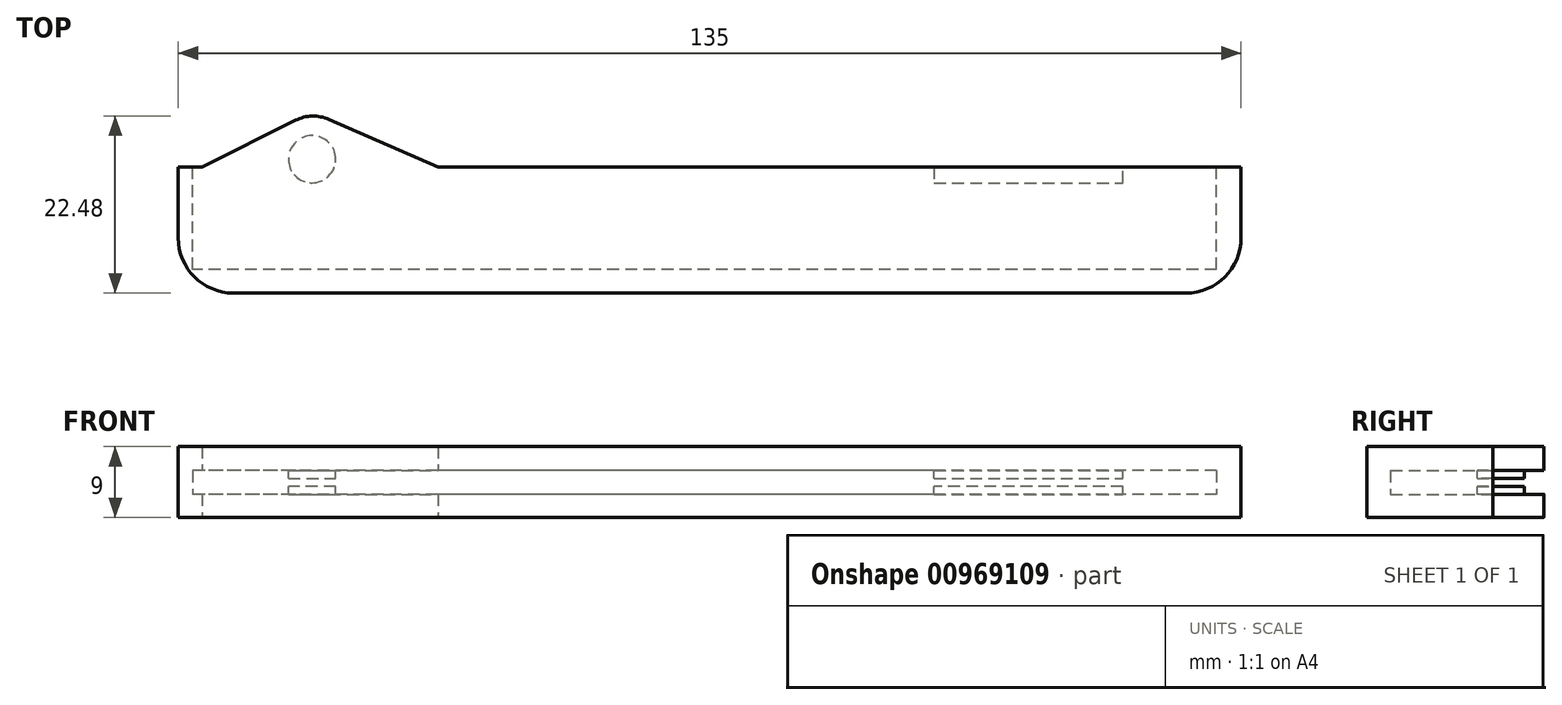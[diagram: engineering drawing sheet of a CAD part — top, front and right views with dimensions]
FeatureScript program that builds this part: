
annotation { "Feature Type Name" : "Feature", "Feature Type Description" : "" }
export const myFeature = defineFeature(function(context is Context, id is Id, definition is map)
    precondition{}
    {
        {
            var Q0;
            Q0=qCreatedBy(makeId("Top.planeOp"),FACE);
            var sketch = newSketch(context, id + "F0", { "sketchPlane" : qUnion([Q0])});
            skLineSegment(sketch, "E0.bottom", {"start": v(-67.5, 11.5) * mm, "end": v(67.5, 11.5) * mm});
            skLineSegment(sketch, "E0.top", {"start": v(-67.5, -11.5) * mm, "end": v(67.5, -11.5) * mm});
            skLineSegment(sketch, "E0.left", {"start": v(-67.5, 11.5) * mm, "end": v(-67.5, -11.5) * mm});
            skLineSegment(sketch, "E0.right", {"start": v(67.5, 11.5) * mm, "end": v(67.5, -11.5) * mm});
            skPoint(sketch, "E0.middle", {"position": v(0, 0) * mm});
            skLineSegment(sketch, "E1", {"start": v(67.5, 4.5) * mm, "end": v(-67.5, 4.5) * mm});
            skLineSegment(sketch, "E2", {"start": v(-50.5, 11.5) * mm, "end": v(-34.5, 4.5) * mm});
            skLineSegment(sketch, "E3", {"start": v(-50.5, 11.5) * mm, "end": v(-64.5, 4.5) * mm});
            skSolve(sketch);
        }
        {
            var Q0;
            {var subQ1=sQuery(id+"F0.wireOp",EDGE,"E0.top");Q0=makeQuery(id+"F0.imprint","IMPRINT",FACE,{"disambiguationData":[TD([[makeQuery(id+"F0.imprint","IMPRINT",EDGE,{"derivedFrom":subQ1}),1.0]])]});}
            var Q1;
            {var subQ2=sQuery(id+"F0.wireOp",EDGE,"E2");Q1=makeQuery(id+"F0.imprint","IMPRINT",FACE,{"disambiguationData":[TD([[makeQuery(id+"F0.imprint","IMPRINT",EDGE,{"derivedFrom":subQ2}),-1.0]])]});}
            extrude(context, id + "F1", {"entities" : qUnion([Q0, Q1]), "depth" : 9 * mm, "offsetDistance" : 25 * mm});
        }
        {
            var Q0;
            {var subQ0=sQuery(id+"F0.wireOp",EDGE,"E1");Q0=makeQuery(id+"F1.opExtrude","SWEPT_FACE",FACE,{"disambiguationData":[OSD([subQ0]),TDD([makeQuery(id+"F0.imprint","IMPRINT",EDGE,{"disambiguationData":[TD([[makeQuery(id+"F0.imprint","INTERSECT",VERTEX,{"derivedFrom":[sQuery(id+"F0.wireOp",EDGE,"E0.right"),subQ0]}),-1.0]])],"derivedFrom":subQ0})])]});}
            var sketch = newSketch(context, id + "F2", { "sketchPlane" : qUnion([Q0])});
            skLineSegment(sketch, "E4.bottom", {"start": v(-64.39, 5.94) * mm, "end": v(65.7, 5.94) * mm});
            skLineSegment(sketch, "E4.top", {"start": v(-64.39, 2.94) * mm, "end": v(65.7, 2.94) * mm});
            skLineSegment(sketch, "E4.left", {"start": v(-64.39, 5.94) * mm, "end": v(-64.39, 2.94) * mm});
            skLineSegment(sketch, "E4.right", {"start": v(65.7, 5.94) * mm, "end": v(65.7, 2.94) * mm});
            skSolve(sketch);
        }
        {
            var Q0;
            Q0 = qSketchRegion(id + "F2", true);
            extrude(context, id + "F3", {"entities" : qUnion([Q0]), "operationType" : NewBodyOperationType.REMOVE, "oppositeDirection" : true, "depth" : 13 * mm, "offsetDistance" : 25 * mm});
        }
        {
            var Q0;
            Q0=makeQuery(id+"F3.boolean.opBoolean","COPY",FACE,{"derivedFrom":makeQuery(id+"F3.opExtrude","CAP_FACE",FACE,{"disambiguationData":[OSD([sQuery(id+"F2.wireOp",EDGE,"E4.bottom"),sQuery(id+"F2.wireOp",EDGE,"E4.top"),sQuery(id+"F2.wireOp",EDGE,"E4.left"),sQuery(id+"F2.wireOp",EDGE,"E4.right")])],"isStart":false})});
            extrude(context, id + "F4", {"entities" : qUnion([Q0]), "operationType" : NewBodyOperationType.REMOVE, "depth" : 25 * mm, "offsetDistance" : 25 * mm});
        }
        {
            var Q0;
            {var subQ0=sQuery(id+"F2.wireOp",EDGE,"E4.bottom");Q0=makeQuery(id+"F4.boolean.opBoolean","MERGE",FACE,{"derivedFrom":[makeQuery(id+"F3.boolean.opBoolean","COPY",FACE,{"derivedFrom":makeQuery(id+"F3.opExtrude","SWEPT_FACE",FACE,{"disambiguationData":[OSD([subQ0])]})})],"fromTools":[makeQuery(id+"F4.opExtrude","SWEPT_FACE",FACE,{"disambiguationData":[OSD([subQ0])]})]});}
            var sketch = newSketch(context, id + "F5", { "sketchPlane" : qUnion([Q0])});
            skLineSegment(sketch, "E5", {"start": v(52.5, -4.5) * mm, "end": v(52.5, 7.04) * mm, "construction": true});
            skLineSegment(sketch, "E6", {"start": v(28.5, -4.5) * mm, "end": v(28.5, 11.64) * mm});
            skLineSegment(sketch, "E7", {"start": v(28.5, -2.5) * mm, "end": v(52.5, -2.5) * mm});
            skLineSegment(sketch, "E8.top", {"start": v(28.5, -4.5) * mm, "end": v(52.5, -4.5) * mm});
            skLineSegment(sketch, "E8.left", {"start": v(28.5, -2.5) * mm, "end": v(28.5, -4.5) * mm});
            skLineSegment(sketch, "E8.right", {"start": v(52.5, -2.5) * mm, "end": v(52.5, -4.5) * mm});
            skSolve(sketch);
        }
        {
            var Q0;
            {var subQ0=sQuery(id+"F5.wireOp",EDGE,"E7");Q0=makeQuery(id+"F5.imprint","IMPRINT",FACE,{"disambiguationData":[TD([[makeQuery(id+"F5.imprint","IMPRINT",EDGE,{"derivedFrom":subQ0}),-1.0]])]});}
            extrude(context, id + "F6", {"entities" : qUnion([Q0]), "operationType" : NewBodyOperationType.ADD, "depth" : 3 * mm, "offsetDistance" : 25 * mm});
        }
        {
            var Q0;
            {var subQ0=sQuery(id+"F0.wireOp",EDGE,"E1");Q0=makeQuery(id+"F6.boolean.opBoolean","MERGE",FACE,{"derivedFrom":[makeQuery(id+"F1.opExtrude","SWEPT_FACE",FACE,{"disambiguationData":[OSD([subQ0]),TDD([makeQuery(id+"F0.imprint","IMPRINT",EDGE,{"disambiguationData":[TD([[makeQuery(id+"F0.imprint","INTERSECT",VERTEX,{"derivedFrom":[sQuery(id+"F0.wireOp",EDGE,"E0.right"),subQ0]}),-1.0]])],"derivedFrom":subQ0})])]}),makeQuery(id+"F6.opExtrude","SWEPT_FACE",FACE,{"disambiguationData":[OSD([sQuery(id+"F5.wireOp",EDGE,"E8.top")])]})]});}
            var sketch = newSketch(context, id + "F7", { "sketchPlane" : qUnion([Q0])});
            skLineSegment(sketch, "E9", {"start": v(-52.5, 4.94) * mm, "end": v(-28.5, 4.94) * mm});
            skLineSegment(sketch, "E10", {"start": v(-28.5, 3.94) * mm, "end": v(-52.5, 3.94) * mm});
            skLineSegment(sketch, "E11", {"start": v(-28.5, 4.94) * mm, "end": v(65, 4.94) * mm});
            skLineSegment(sketch, "E12", {"start": v(65, 4.94) * mm, "end": v(65, 3.94) * mm});
            skLineSegment(sketch, "E13", {"start": v(65, 3.94) * mm, "end": v(-28.5, 3.94) * mm});
            skSolve(sketch);
        }
        {
            var Q0;
            {var subQ0=sQuery(id+"F2.wireOp",EDGE,"E4.bottom");Q0=makeQuery(id+"F4.boolean.opBoolean","MERGE",FACE,{"derivedFrom":[makeQuery(id+"F3.boolean.opBoolean","COPY",FACE,{"derivedFrom":makeQuery(id+"F3.opExtrude","SWEPT_FACE",FACE,{"disambiguationData":[OSD([subQ0])]})})],"fromTools":[makeQuery(id+"F4.opExtrude","SWEPT_FACE",FACE,{"disambiguationData":[OSD([subQ0])]})]});}
            var sketch = newSketch(context, id + "F8", { "sketchPlane" : qUnion([Q0])});
            skCircle(sketch, "E14", {"center": v(-50.5, -5.5) * mm, "radius": 3 * mm});
            skSolve(sketch);
        }
        {
            var Q0;
            Q0=makeQuery(id+"F8.imprint","IMPRINT",FACE,{"disambiguationData":[TD([[makeQuery(id+"F8.imprint","IMPRINT",EDGE,{"derivedFrom":sQuery(id+"F8.wireOp",EDGE,"E14")}),1.0]])]});
            extrude(context, id + "F9", {"entities" : qUnion([Q0]), "operationType" : NewBodyOperationType.ADD, "depth" : 4 * mm, "offsetDistance" : 25 * mm});
        }
        {
            var Q0;
            {var subQ0=sQuery(id+"F7.wireOp",EDGE,"E9");Q0=makeQuery(id+"F7.imprint","IMPRINT",FACE,{"disambiguationData":[TD([[makeQuery(id+"F7.imprint","IMPRINT",EDGE,{"derivedFrom":subQ0}),-1.0]])]});}
            var Q1;
            {var subQ0=sQuery(id+"F7.wireOp",EDGE,"E11");Q1=makeQuery(id+"F7.imprint","IMPRINT",FACE,{"disambiguationData":[TD([[makeQuery(id+"F7.imprint","IMPRINT",EDGE,{"derivedFrom":subQ0}),-1.0]])]});}
            extrude(context, id + "F10", {"entities" : qUnion([Q0, Q1]), "operationType" : NewBodyOperationType.REMOVE, "oppositeDirection" : true, "depth" : 10 * mm, "offsetDistance" : 25 * mm});
        }
        {
            var Q0;
            {var subQ0=sQuery(id+"F7.wireOp",EDGE,"E11");Q0=makeQuery(id+"F7.imprint","IMPRINT",FACE,{"disambiguationData":[TD([[makeQuery(id+"F7.imprint","IMPRINT",EDGE,{"derivedFrom":subQ0}),-1.0]])]});}
            extrude(context, id + "F11", {"entities" : qUnion([Q0]), "operationType" : NewBodyOperationType.REMOVE, "depth" : 25 * mm, "offsetDistance" : 25 * mm});
        }
        {
            var Q0;
            {var subQ0=sQuery(id+"F0.wireOp",EDGE,"E3");var subQ1=sQuery(id+"F2.wireOp",EDGE,"E4.top");var subQ2=sQuery(id+"F0.wireOp",EDGE,"E2");Q0=makeQuery(id+"F4.boolean.opBoolean","SPLIT",EDGE,{"disambiguationData":[TD([makeQuery(id+"F3.boolean.opBoolean","COPY",FACE,{"derivedFrom":makeQuery(id+"F3.opExtrude","SWEPT_FACE",FACE,{"disambiguationData":[OSD([subQ1])]})})])],"derivedFrom":makeQuery(id+"F1.opExtrude","SWEPT_EDGE",EDGE,{"disambiguationData":[OSD([sQuery(id+"F0.wireOp",EDGE,"E0.bottom"),subQ2,subQ0])]})});}
            var Q1;
            {var subQ0=sQuery(id+"F2.wireOp",EDGE,"E4.bottom");var subQ1=sQuery(id+"F0.wireOp",EDGE,"E3");var subQ2=sQuery(id+"F0.wireOp",EDGE,"E2");Q1=makeQuery(id+"F4.boolean.opBoolean","SPLIT",EDGE,{"disambiguationData":[TD([makeQuery(id+"F3.boolean.opBoolean","COPY",FACE,{"derivedFrom":makeQuery(id+"F3.opExtrude","SWEPT_FACE",FACE,{"disambiguationData":[OSD([subQ0])]})})])],"derivedFrom":makeQuery(id+"F1.opExtrude","SWEPT_EDGE",EDGE,{"disambiguationData":[OSD([sQuery(id+"F0.wireOp",EDGE,"E0.bottom"),subQ2,subQ1])]})});}
            fillet(context, id + "F12", {"entities" : qUnion([Q0, Q1]), "radius" : 5 * mm, "tangentPropagation" : true, "allowEdgeOverflow" : false});
        }
        {
            var Q0;
            Q0=makeQuery(id+"F1.opExtrude","SWEPT_EDGE",EDGE,{"disambiguationData":[OSD([sQuery(id+"F0.wireOp",EDGE,"E0.top"),sQuery(id+"F0.wireOp",EDGE,"E0.left")])]});
            var Q1;
            Q1=makeQuery(id+"F1.opExtrude","SWEPT_EDGE",EDGE,{"disambiguationData":[OSD([sQuery(id+"F0.wireOp",EDGE,"E0.top"),sQuery(id+"F0.wireOp",EDGE,"E0.right")])]});
            fillet(context, id + "F13", {"entities" : qUnion([Q0, Q1]), "radius" : 7 * mm, "tangentPropagation" : true, "allowEdgeOverflow" : false});
        }
    });
